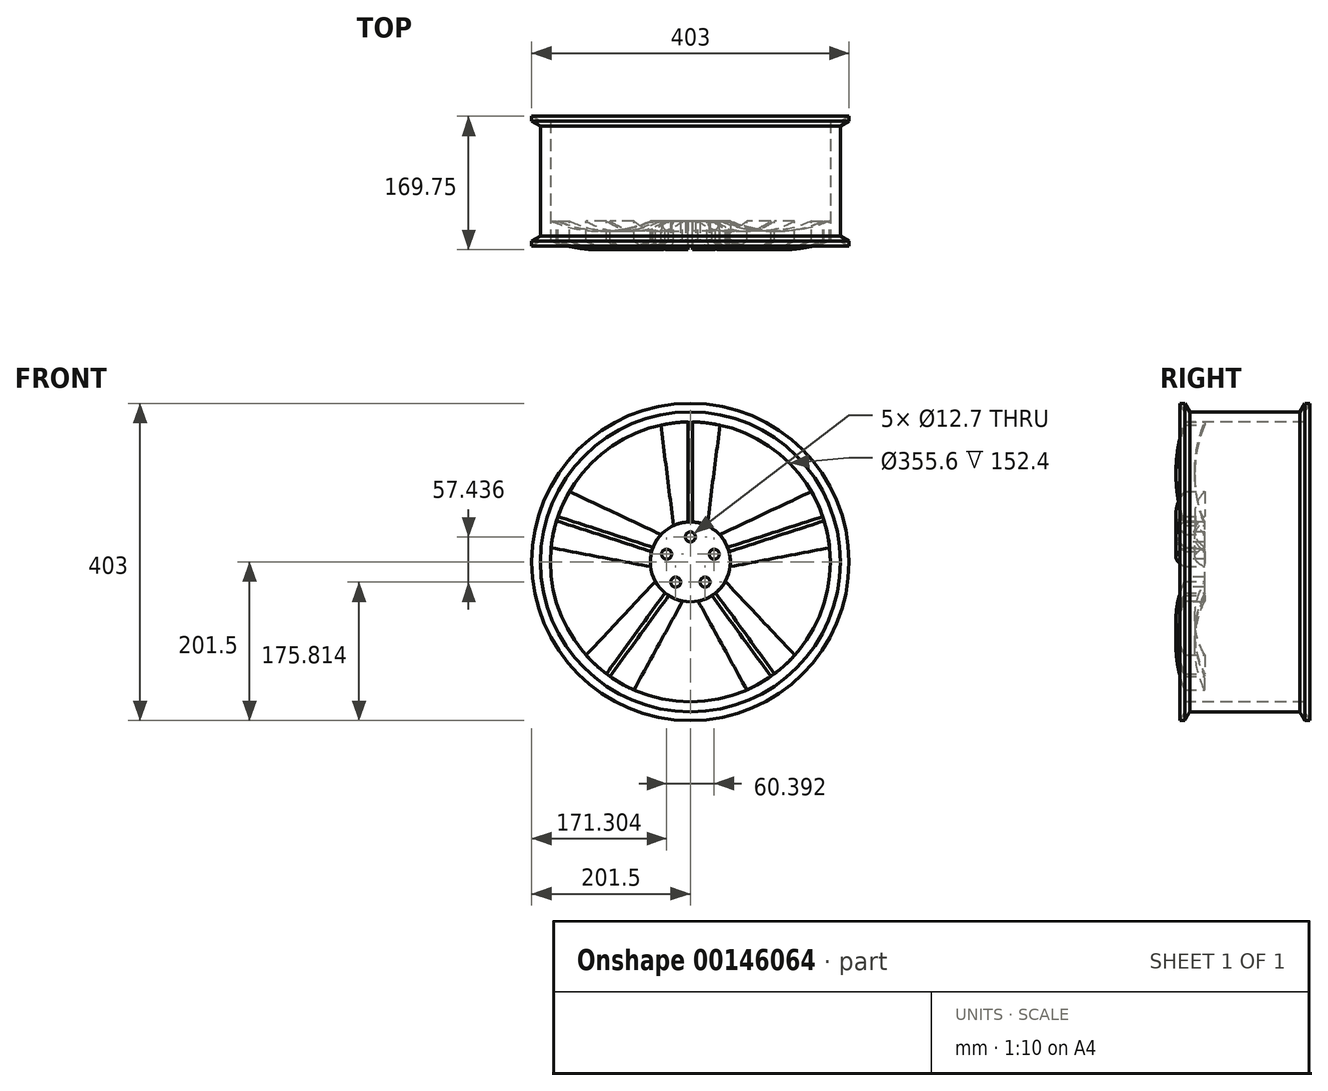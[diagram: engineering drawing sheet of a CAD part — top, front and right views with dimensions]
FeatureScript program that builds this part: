
annotation { "Feature Type Name" : "Feature", "Feature Type Description" : "" }
export const myFeature = defineFeature(function(context is Context, id is Id, definition is map)
    precondition{}
    {
        {
            var Q0;
            Q0=qCreatedBy(makeId("Right.planeOp"),FACE);
            var sketch = newSketch(context, id + "F0", { "sketchPlane" : qUnion([Q0])});
            skLineSegment(sketch, "E0.bottom", {"start": v(0, 0) * mm, "end": v(152.4, 0) * mm});
            skLineSegment(sketch, "E0.top", {"start": v(0, 177.8) * mm, "end": v(152.4, 177.8) * mm});
            skLineSegment(sketch, "E0.left", {"start": v(0, 0) * mm, "end": v(0, 177.8) * mm});
            skLineSegment(sketch, "E0.right", {"start": v(152.4, 0) * mm, "end": v(152.4, 177.8) * mm});
            skLineSegment(sketch, "E1", {"start": v(0, 177.8) * mm, "end": v(0, 190.5) * mm});
            skLineSegment(sketch, "E2", {"start": v(0, 190.5) * mm, "end": v(-6.35, 201.5) * mm});
            skLineSegment(sketch, "E3", {"start": v(-6.35, 201.5) * mm, "end": v(158.75, 201.5) * mm});
            skLineSegment(sketch, "E4", {"start": v(152.4, 177.8) * mm, "end": v(152.4, 190.5) * mm});
            skLineSegment(sketch, "E5", {"start": v(152.4, 190.5) * mm, "end": v(158.75, 201.5) * mm});
            skLineSegment(sketch, "E6", {"start": v(0, 201.5) * mm, "end": v(6.35, 190.5) * mm});
            skLineSegment(sketch, "E7", {"start": v(152.4, 201.5) * mm, "end": v(146.05, 190.5) * mm});
            skLineSegment(sketch, "E8", {"start": v(6.35, 190.5) * mm, "end": v(146.05, 190.5) * mm});
            skSolve(sketch);
        }
        {
            var Q0;
            Q0=makeQuery(id+"F0.imprint","IMPRINT",FACE,{"disambiguationData":[TD([[makeQuery(id+"F0.imprint","IMPRINT",EDGE,{"derivedFrom":sQuery(id+"F0.wireOp",EDGE,"E0.top")}),1.0]])]});
            var Q1;
            Q1=sQuery(id+"F0.wireOp",EDGE,"E0.bottom");
            revolve(context, id + "F1", {"entities" : qUnion([Q0]), "axis" : qUnion([Q1]), "revolveType" : RevolveType.FULL});
        }
        {
            var Q0;
            Q0=makeQuery(id+"F1.opRevolve","SWEPT_FACE",FACE,{"disambiguationData":[OSD([sQuery(id+"F0.wireOp",EDGE,"E1")])]});
            var sketch = newSketch(context, id + "F2", { "sketchPlane" : qUnion([Q0])});
            skCircle(sketch, "E9", {"center": v(0, 0) * mm, "radius": 50.8 * mm});
            skSolve(sketch);
        }
        {
            var Q0;
            Q0=makeQuery(id+"F2.imprint","IMPRINT",FACE,{"disambiguationData":[TD([[makeQuery(id+"F2.imprint","IMPRINT",EDGE,{"derivedFrom":sQuery(id+"F2.wireOp",EDGE,"E9")}),1.0]])]});
            extrude(context, id + "F3", {"entities" : qUnion([Q0]), "oppositeDirection" : true, "depth" : 25.4 * mm});
        }
        {
            var Q0;
            Q0=makeQuery(id+"F3.opExtrude","CAP_FACE",FACE,{"disambiguationData":[OSD([sQuery(id+"F2.wireOp",EDGE,"E9")])],"isStart":true});
            var sketch = newSketch(context, id + "F4", { "sketchPlane" : qUnion([Q0])});
            skLineSegment(sketch, "E10", {"start": v(0, 50.8) * mm, "end": v(0, 177.79) * mm});
            skLineSegment(sketch, "E11", {"start": v(0, 177.79) * mm, "end": v(38.1, 177.79) * mm});
            skLineSegment(sketch, "E12", {"start": v(38.1, 177.79) * mm, "end": v(21.34, 46.1) * mm});
            skLineSegment(sketch, "E13", {"start": v(21.34, 46.1) * mm, "end": v(2.86, 50.72) * mm});
            skLineSegment(sketch, "E14", {"start": v(2.86, 50.72) * mm, "end": v(2.86, 177.79) * mm});
            skLineSegment(sketch, "E15.MirrorCS", {"start": v(0, 177.79) * mm, "end": v(-38.1, 177.79) * mm});
            skLineSegment(sketch, "E16.MirrorCS", {"start": v(-2.86, 50.72) * mm, "end": v(-2.86, 177.79) * mm});
            skLineSegment(sketch, "E17.MirrorCS", {"start": v(-38.1, 177.79) * mm, "end": v(-21.34, 46.1) * mm});
            skLineSegment(sketch, "E18.MirrorCS", {"start": v(-21.34, 46.1) * mm, "end": v(-2.86, 50.72) * mm});
            skCircle(sketch, "E19", {"center": v(0, 0) * mm, "radius": 50.8 * mm});
            skCircle(sketch, "E20", {"center": v(0, 0) * mm, "radius": 177.79 * mm});
            skSolve(sketch);
        }
        {
            var Q0;
            {var subQ4=sQuery(id+"F4.wireOp",EDGE,"E20");var subQ6=sQuery(id+"F4.wireOp",EDGE,"E17.MirrorCS");var subQ8=makeQuery(id+"F4.imprint","INTERSECT",VERTEX,{"derivedFrom":[subQ6,subQ4]});Q0=makeQuery(id+"F4.imprint","IMPRINT",FACE,{"disambiguationData":[TD([[makeQuery(id+"F4.imprint","IMPRINT",EDGE,{"disambiguationData":[TD([[subQ8,1.0]])],"derivedFrom":subQ4}),1.0]])]});}
            var Q1;
            {var subQ2=sQuery(id+"F4.wireOp",EDGE,"E12");var subQ4=sQuery(id+"F4.wireOp",EDGE,"E20");var subQ5=makeQuery(id+"F4.imprint","INTERSECT",VERTEX,{"derivedFrom":[subQ2,subQ4]});Q1=makeQuery(id+"F4.imprint","IMPRINT",FACE,{"disambiguationData":[TD([[makeQuery(id+"F4.imprint","IMPRINT",EDGE,{"disambiguationData":[TD([[subQ5,-1.0]])],"derivedFrom":subQ4}),1.0]])]});}
            extrude(context, id + "F5", {"entities" : qUnion([Q0, Q1]), "endBound" : BoundingType.SYMMETRIC, "depth" : 50.8 * mm});
        }
        {
            var Q0;
            Q0=makeQuery(id+"F5.opExtrude","SWEPT_BODY",BODY,{"disambiguationData":[OSD([sQuery(id+"F2.wireOp",EDGE,"E9"),sQuery(id+"F4.wireOp",EDGE,"E11"),sQuery(id+"F4.wireOp",EDGE,"E12"),sQuery(id+"F4.wireOp",EDGE,"E14")])]});
            var Q1;
            Q1=makeQuery(id+"F5.opExtrude","SWEPT_BODY",BODY,{"disambiguationData":[OSD([sQuery(id+"F2.wireOp",EDGE,"E9"),sQuery(id+"F4.wireOp",EDGE,"E15.MirrorCS"),sQuery(id+"F4.wireOp",EDGE,"E16.MirrorCS"),sQuery(id+"F4.wireOp",EDGE,"E17.MirrorCS")])]});
            var Q2;
            Q2=makeQuery(id+"F1.opRevolve","SWEPT_FACE",FACE,{"disambiguationData":[OSD([sQuery(id+"F0.wireOp",EDGE,"E0.top")])]});
            circularPattern(context, id + "F6", {"entities" : qUnion([Q0, Q1]), "axis" : qUnion([Q2]), "angle" : 360 * degree, "instanceCount" : 5, "equalSpace" : true});
        }
        {
            var Q0;
            Q0=qCreatedBy(makeId("Right.planeOp"),FACE);
            var sketch = newSketch(context, id + "F7", { "sketchPlane" : qUnion([Q0])});
            skLineSegment(sketch, "E21", {"start": v(0, 50.8) * mm, "end": v(24.8, 50.8) * mm});
            skLineSegment(sketch, "E22", {"start": v(25.4, -50.8) * mm, "end": v(0, -50.8) * mm});
            skLineSegment(sketch, "E23", {"start": v(0, 177.8) * mm, "end": v(152.4, 177.8) * mm});
            skLineSegment(sketch, "E24", {"start": v(152.4, -177.8) * mm, "end": v(0, -177.8) * mm});
            skLineSegment(sketch, "E25", {"start": v(0, 50.8) * mm, "end": v(-104.1, 50.8) * mm});
            skLineSegment(sketch, "E26", {"start": v(-104.1, 50.8) * mm, "end": v(-104.1, 177.8) * mm});
            skLineSegment(sketch, "E27", {"start": v(-104.1, 177.8) * mm, "end": v(0, 177.8) * mm});
            skLineSegment(sketch, "E28", {"start": v(0, 50.8) * mm, "end": v(25.4, 50.8) * mm});
            skArc(sketch, "E29", {"start": v(25.4, 177.8) * mm, "mid": v(12.7, 114.3) * mm, "end": v(25.4, 50.8) * mm});
            skLineSegment(sketch, "E30", {"start": v(25.4, 50.8) * mm, "end": v(25.4, 177.8) * mm});
            skArc(sketch, "E31", {"start": v(0, 177.8) * mm, "mid": v(-11, 114.3) * mm, "end": v(0, 50.8) * mm});
            skSolve(sketch);
        }
        {
            var Q0;
            Q0=makeQuery(id+"F7.imprint","IMPRINT",FACE,{"disambiguationData":[TD([[makeQuery(id+"F7.imprint","IMPRINT",EDGE,{"derivedFrom":sQuery(id+"F7.wireOp",EDGE,"E25")}),-1.0]])]});
            var Q1;
            Q1=makeQuery(id+"F7.imprint","IMPRINT",FACE,{"disambiguationData":[TD([[makeQuery(id+"F7.imprint","IMPRINT",EDGE,{"derivedFrom":sQuery(id+"F7.wireOp",EDGE,"E29")}),1.0]])]});
            var Q2;
            Q2=makeQuery(id+"F1.opRevolve","SWEPT_FACE",FACE,{"disambiguationData":[OSD([sQuery(id+"F0.wireOp",EDGE,"E0.top")])]});
            revolve(context, id + "F8", {"operationType" : NewBodyOperationType.REMOVE, "entities" : qUnion([Q0, Q1]), "axis" : qUnion([Q2]), "revolveType" : RevolveType.FULL, "oppositeDirection" : true});
        }
        {
            var Q0;
            Q0=makeQuery(id+"F3.opExtrude","CAP_FACE",FACE,{"disambiguationData":[OSD([sQuery(id+"F2.wireOp",EDGE,"E9")])],"isStart":true});
            var sketch = newSketch(context, id + "F9", { "sketchPlane" : qUnion([Q0])});
            skLineSegment(sketch, "E32", {"start": v(0, 0) * mm, "end": v(0, 31.75) * mm});
            skCircle(sketch, "E33", {"center": v(0, 31.75) * mm, "radius": 6.35 * mm});
            skCircle(sketch, "E34.1.0", {"center": v(-30.2, 9.81) * mm, "radius": 6.35 * mm});
            skCircle(sketch, "E34.2.0", {"center": v(-18.66, -25.69) * mm, "radius": 6.35 * mm});
            skCircle(sketch, "E34.3.0", {"center": v(18.66, -25.69) * mm, "radius": 6.35 * mm});
            skCircle(sketch, "E34.4.0", {"center": v(30.2, 9.81) * mm, "radius": 6.35 * mm});
            skPoint(sketch, "E34.center", {"position": v(0, 0) * mm});
            skSolve(sketch);
        }
        {
            var Q0;
            Q0=makeQuery(id+"F9.imprint","IMPRINT",FACE,{"disambiguationData":[TD([[makeQuery(id+"F9.imprint","IMPRINT",EDGE,{"derivedFrom":sQuery(id+"F9.wireOp",EDGE,"E33")}),1.0]])]});
            var Q1;
            Q1=makeQuery(id+"F9.imprint","IMPRINT",FACE,{"disambiguationData":[TD([[makeQuery(id+"F9.imprint","IMPRINT",EDGE,{"derivedFrom":sQuery(id+"F9.wireOp",EDGE,"E34.4.0")}),1.0]])]});
            var Q2;
            Q2=makeQuery(id+"F9.imprint","IMPRINT",FACE,{"disambiguationData":[TD([[makeQuery(id+"F9.imprint","IMPRINT",EDGE,{"derivedFrom":sQuery(id+"F9.wireOp",EDGE,"E34.3.0")}),1.0]])]});
            var Q3;
            Q3=makeQuery(id+"F9.imprint","IMPRINT",FACE,{"disambiguationData":[TD([[makeQuery(id+"F9.imprint","IMPRINT",EDGE,{"derivedFrom":sQuery(id+"F9.wireOp",EDGE,"E34.2.0")}),1.0]])]});
            var Q4;
            Q4=makeQuery(id+"F9.imprint","IMPRINT",FACE,{"disambiguationData":[TD([[makeQuery(id+"F9.imprint","IMPRINT",EDGE,{"derivedFrom":sQuery(id+"F9.wireOp",EDGE,"E34.1.0")}),1.0]])]});
            extrude(context, id + "F10", {"entities" : qUnion([Q0, Q1, Q2, Q3, Q4]), "operationType" : NewBodyOperationType.REMOVE, "endBound" : BoundingType.UP_TO_NEXT, "oppositeDirection" : true, "depth" : 25.4 * mm});
        }
    });
